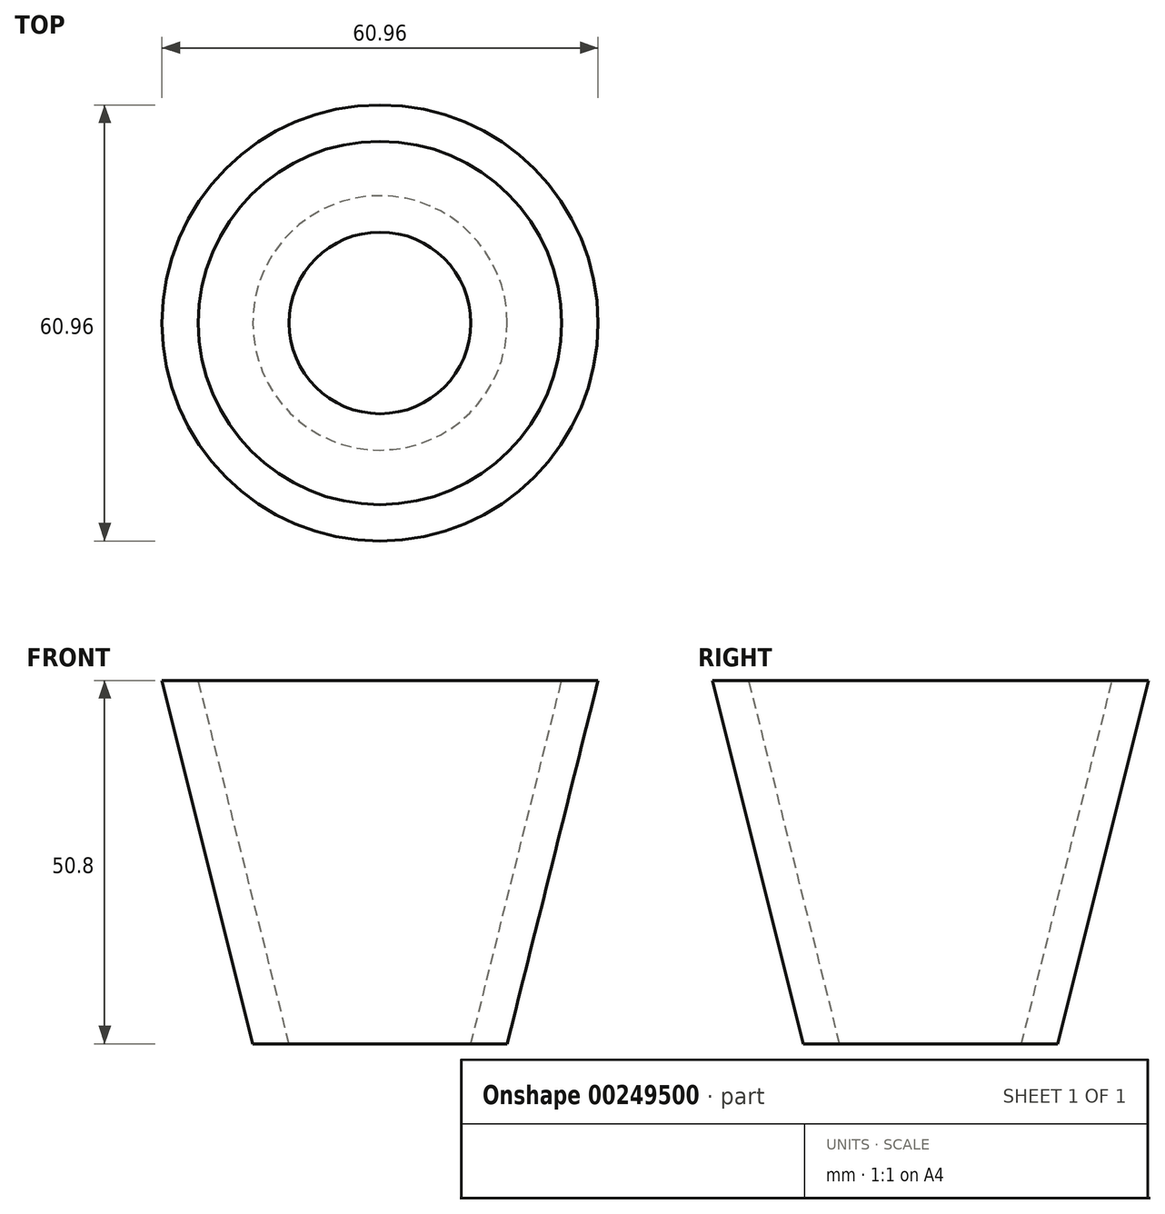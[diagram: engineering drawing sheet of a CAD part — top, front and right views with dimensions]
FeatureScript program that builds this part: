
annotation { "Feature Type Name" : "Feature", "Feature Type Description" : "" }
export const myFeature = defineFeature(function(context is Context, id is Id, definition is map)
    precondition{}
    {
        {
            var Q0;
            Q0=qCreatedBy(makeId("Front.planeOp"),FACE);
            var sketch = newSketch(context, id + "F0", { "sketchPlane" : qUnion([Q0])});
            skLineSegment(sketch, "E0", {"start": v(0, 25.4) * mm, "end": v(0, -25.4) * mm, "construction": true});
            skLineSegment(sketch, "E1", {"start": v(0, 25.4) * mm, "end": v(25.4, 25.4) * mm, "construction": true});
            skLineSegment(sketch, "E2", {"start": v(0, -25.4) * mm, "end": v(12.7, -25.4) * mm, "construction": true});
            skLineSegment(sketch, "E3", {"start": v(25.4, 25.4) * mm, "end": v(12.7, -25.4) * mm});
            skLineSegment(sketch, "E4", {"start": v(25.4, 25.4) * mm, "end": v(30.48, 25.4) * mm});
            skLineSegment(sketch, "E5", {"start": v(12.7, -25.4) * mm, "end": v(17.78, -25.4) * mm});
            skLineSegment(sketch, "E6", {"start": v(30.48, 25.4) * mm, "end": v(17.78, -25.4) * mm});
            skSolve(sketch);
        }
        {
            var Q0;
            Q0=makeQuery(id+"F0.imprint","IMPRINT",FACE,{"disambiguationData":[TD([[makeQuery(id+"F0.imprint","IMPRINT",EDGE,{"derivedFrom":sQuery(id+"F0.wireOp",EDGE,"E3")}),1.0]])]});
            var Q1;
            Q1=sQuery(id+"F0.wireOp",EDGE,"E0");
            revolve(context, id + "F1", {"entities" : qUnion([Q0]), "axis" : qUnion([Q1]), "revolveType" : RevolveType.FULL});
        }
    });
